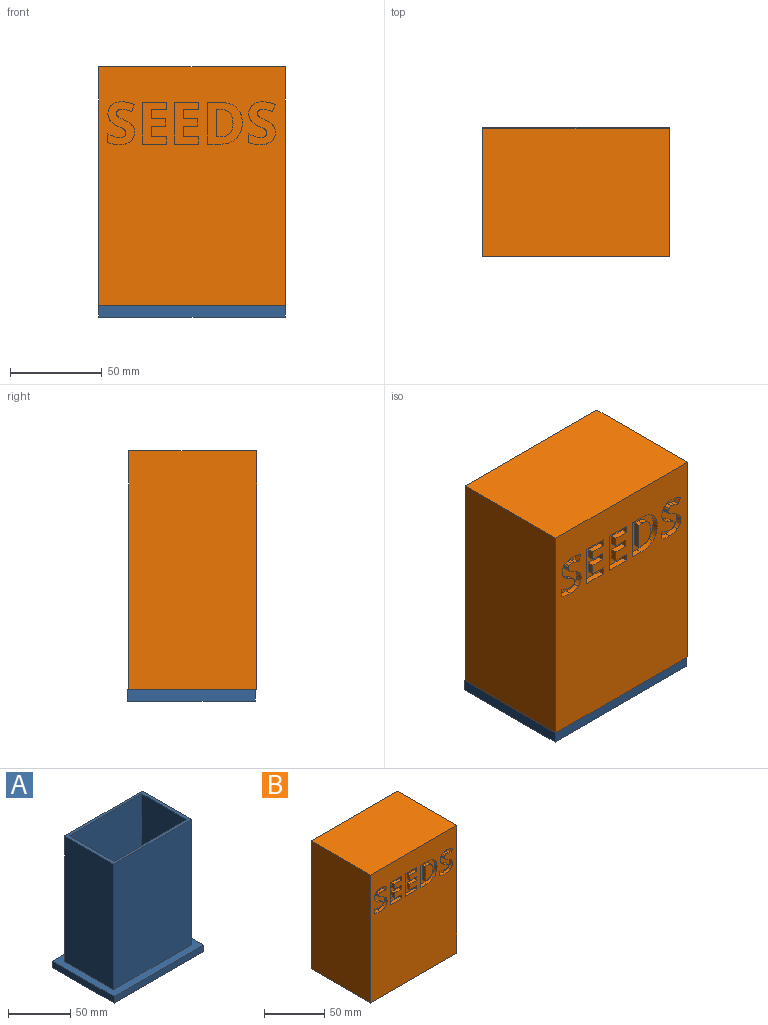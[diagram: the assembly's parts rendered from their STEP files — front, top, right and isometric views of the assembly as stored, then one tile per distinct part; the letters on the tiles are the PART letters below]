
ASSEMBLY  parts=2 mates=1
PART A: 16 faces, bbox 101.6x69.9x130.2 mm
  f0: plane 88.65x55.88mm, normal (0,0,1), area 760mm2, adj f1,f2,f3,f4,f11,f12,f14,f15
  f1: plane 123.83x55.88mm, normal (-1,0,0), area 6919.3mm2, adj f0,f3,f4,f5
  f2: plane 123.83x55.88mm, normal (1,0,0), area 6919.3mm2, adj f0,f3,f4,f5
  f3: plane 123.83x88.65mm, normal (0,-1,0), area 10976.6mm2, adj f0,f1,f2,f5
  f4: plane 123.83x88.65mm, normal (0,1,0), area 10976.6mm2, adj f0,f1,f2,f5
  f5: plane 101.6x69.85mm, normal (0,0,1), area 2143.2mm2, adj f1,f2,f3,f4,f6,f8,f9,f10
  f6: plane 69.85x6.35mm, normal (-1,0,0), area 443.5mm2, adj f5,f7,f9,f10
  f7: plane 101.6x69.85mm, normal (0,0,-1), area 7096.8mm2, adj f6,f8,f9,f10
  f8: plane 69.85x6.35mm, normal (1,0,0), area 443.5mm2, adj f5,f7,f9,f10
  f9: plane 101.6x6.35mm, normal (0,-1,0), area 645.2mm2, adj f5,f6,f7,f8
  f10: plane 101.6x6.35mm, normal (0,1,0), area 645.2mm2, adj f5,f6,f7,f8
  f11: plane 123.83x50.8mm, normal (-1,0,0), area 6290.3mm2, adj f0,f13,f14,f15
  f12: plane 123.83x50.8mm, normal (1,0,0), area 6290.3mm2, adj f0,f13,f14,f15
  f13: plane 82.55x50.8mm, normal (0,0,1), area 4193.5mm2, adj f11,f12,f14,f15
  f14: plane 123.83x82.55mm, normal (0,1,0), area 10221.8mm2, adj f0,f11,f12,f13
  f15: plane 123.83x82.55mm, normal (0,-1,0), area 10221.8mm2, adj f0,f11,f12,f13
PART B: 109 faces, bbox 101.6x69.9x130.2 mm
  f0: plane 130.18x101.6mm, normal (0,-1,0), area 12041.5mm2, adj f1,f2,f3,f4,f11,f12,f13,f14
  f1: plane 101.6x69.85mm, normal (0,0,-1), area 2016.1mm2, adj f0,f2,f4,f5,f6,f8,f9,f10
  f2: plane 130.18x69.85mm, normal (1,0,0), area 9092.7mm2, adj f0,f1,f3,f5
  f3: plane 101.6x69.85mm, normal (0,0,1), area 7096.8mm2, adj f0,f2,f4,f5
  f4: plane 130.18x69.85mm, normal (-1,0,0), area 9092.7mm2, adj f0,f1,f3,f5
  f5: plane 130.18x101.6mm, normal (0,1,0), area 13225.8mm2, adj f1,f2,f3,f4
  f6: plane 123.83x57.15mm, normal (-1,0,0), area 7076.6mm2, adj f1,f7,f9,f10
  f7: plane 88.9x57.15mm, normal (0,0,-1), area 5080.6mm2, adj f6,f8,f9,f10
  f8: plane 123.83x57.15mm, normal (1,0,0), area 7076.6mm2, adj f1,f7,f9,f10
  f9: plane 123.83x88.9mm, normal (0,-1,0), area 11008mm2, adj f1,f6,f7,f8
  f10: plane 123.83x88.9mm, normal (0,1,0), area 11008mm2, adj f1,f6,f7,f8
  f11: extruded ~4.86x3.18mm, area 17.6mm2, adj f0,f12,f38,f39
  f12: extruded ~3.76x3.18mm, area 12.7mm2, adj f0,f11,f13,f39
  f13: extruded ~4.38x3.18mm, area 17.1mm2, adj f0,f12,f14,f39
  f14: extruded ~3.18x3.06mm, area 11mm2, adj f0,f13,f15,f39
  f15: extruded ~3.18x0.94mm, area 4.2mm2, adj f0,f14,f16,f39
  f16: extruded ~3.18x1.11mm, area 3.7mm2, adj f0,f15,f17,f39
  f17: extruded ~3.18x1.66mm, area 6mm2, adj f0,f16,f18,f39
  f18: extruded ~3.18x2.1mm, area 7.1mm2, adj f0,f17,f19,f39
  f19: extruded ~3.18x2.34mm, area 7.5mm2, adj f0,f18,f20,f39
  f20: extruded ~3.18x3.01mm, area 10.1mm2, adj f0,f19,f21,f39
  f21: plane 3.76x3.18mm, normal (-0.92,0,0.38), area 12.9mm2, adj f0,f20,f22,f39
  f22: extruded ~3.37x3.18mm, area 11.4mm2, adj f0,f21,f23,f39
  f23: extruded ~3.39x3.18mm, area 10.9mm2, adj f0,f22,f24,f39
  f24: extruded ~5.66x3.18mm, area 19.2mm2, adj f0,f23,f25,f39
  f25: extruded ~4.75x3.18mm, area 17mm2, adj f0,f24,f26,f39
  f26: extruded ~3.18x2.8mm, area 9.2mm2, adj f0,f25,f27,f39
  f27: extruded ~3.18x2.1mm, area 8.6mm2, adj f0,f26,f28,f39
  f28: extruded ~3.18x3.13mm, area 11.6mm2, adj f0,f27,f29,f39
  f29: extruded ~3.18x2.95mm, area 10.6mm2, adj f0,f28,f30,f39
  f30: extruded ~3.18x1.1mm, area 4.8mm2, adj f0,f29,f31,f39
  f31: extruded ~3.18x1.19mm, area 4mm2, adj f0,f30,f32,f39
  f32: extruded ~3.18x1.81mm, area 6.6mm2, adj f0,f31,f33,f39
  f33: extruded ~3.18x2.43mm, area 8.1mm2, adj f0,f32,f34,f39
  f34: extruded ~3.18x2.92mm, area 9.4mm2, adj f0,f33,f35,f39
  f35: extruded ~3.9x3.18mm, area 13.2mm2, adj f0,f34,f36,f39
  f36: plane 4.48x3.18mm, normal (1,0,0), area 14.2mm2, adj f0,f35,f37,f39
  f37: extruded ~6.45x3.18mm, area 21.1mm2, adj f0,f36,f38,f39
  f38: extruded ~6.17x3.18mm, area 20.8mm2, adj f0,f11,f37,f39
  f39: plane 23.4x14.84mm, normal (0,-1,0), area 195.4mm2, adj f11,f12,f13,f14,f15,f16,f17,f18
  f40: extruded ~7.33x6.48mm, area 35.6mm2, adj f41,f51,f52,f108
  f41: extruded ~7.49x6.98mm, area 37.3mm2, adj f40,f42,f52,f108
  f42: plane 3.18x2.07mm, normal (0,0,-1), area 6.6mm2, adj f41,f43,f52,f108
  f43: plane 14.82x3.18mm, normal (-1,0,0), area 47.1mm2, adj f42,f51,f52,f108
  f44: extruded ~8.61x3.2mm, area 30mm2, adj f0,f45,f50,f52
  f45: extruded ~8.22x3.18mm, area 28.7mm2, adj f0,f44,f46,f52
  f46: extruded ~8.66x3.18mm, area 29.8mm2, adj f0,f45,f47,f52
  f47: plane 7.14x3.18mm, normal (0,0,-1), area 22.7mm2, adj f0,f46,f48,f52
  f48: plane 22.76x3.18mm, normal (1,0,0), area 72.3mm2, adj f0,f47,f49,f52
  f49: plane 6.45x3.18mm, normal (0,0,1), area 20.5mm2, adj f0,f48,f50,f52
  f50: extruded ~9.24x3.18mm, area 31.6mm2, adj f0,f44,f49,f52
  f51: plane 3.18x2.57mm, normal (0,0,1), area 8.1mm2, adj f40,f43,f52,f108
  f52: plane 22.76x18.89mm, normal (0,-1,0), area 263.8mm2, adj f40,f41,f42,f43,f44,f45,f46,f47
  f53: plane 13.11x3.18mm, normal (0,0,1), area 41.6mm2, adj f0,f54,f64,f65
  f54: plane 3.99x3.18mm, normal (-1,0,0), area 12.7mm2, adj f0,f53,f55,f65
  f55: plane 8.28x3.18mm, normal (0,0,-1), area 26.3mm2, adj f0,f54,f56,f65
  f56: plane 5.87x3.18mm, normal (-1,0,0), area 18.6mm2, adj f0,f55,f57,f65
  f57: plane 7.71x3.18mm, normal (0,0,1), area 24.5mm2, adj f0,f56,f58,f65
  f58: plane 3.96x3.18mm, normal (-1,0,0), area 12.6mm2, adj f0,f57,f59,f65
  f59: plane 7.71x3.18mm, normal (0,0,-1), area 24.5mm2, adj f0,f58,f60,f65
  f60: plane 5x3.18mm, normal (-1,0,0), area 15.9mm2, adj f0,f59,f61,f65
  f61: plane 8.28x3.18mm, normal (0,0,1), area 26.3mm2, adj f0,f60,f62,f65
  f62: plane 3.96x3.18mm, normal (-1,0,0), area 12.6mm2, adj f0,f61,f63,f65
  f63: plane 13.11x3.18mm, normal (0,0,-1), area 41.6mm2, adj f0,f62,f64,f65
  f64: plane 22.76x3.18mm, normal (1,0,0), area 72.3mm2, adj f0,f53,f63,f65
  f65: plane 22.76x13.11mm, normal (0,-1,0), area 206.1mm2, adj f53,f54,f55,f56,f57,f58,f59,f60
  f66: plane 13.11x3.18mm, normal (0,0,1), area 41.6mm2, adj f0,f67,f77,f78
  f67: plane 3.99x3.18mm, normal (-1,0,0), area 12.7mm2, adj f0,f66,f68,f78
  f68: plane 8.28x3.18mm, normal (0,0,-1), area 26.3mm2, adj f0,f67,f69,f78
  f69: plane 5.87x3.18mm, normal (-1,0,0), area 18.6mm2, adj f0,f68,f70,f78
  f70: plane 7.71x3.18mm, normal (0,0,1), area 24.5mm2, adj f0,f69,f71,f78
  f71: plane 3.96x3.18mm, normal (-1,0,0), area 12.6mm2, adj f0,f70,f72,f78
  f72: plane 7.71x3.18mm, normal (0,0,-1), area 24.5mm2, adj f0,f71,f73,f78
  f73: plane 5x3.18mm, normal (-1,0,0), area 15.9mm2, adj f0,f72,f74,f78
  f74: plane 8.28x3.18mm, normal (0,0,1), area 26.3mm2, adj f0,f73,f75,f78
  f75: plane 3.96x3.18mm, normal (-1,0,0), area 12.6mm2, adj f0,f74,f76,f78
  f76: plane 13.11x3.18mm, normal (0,0,-1), area 41.6mm2, adj f0,f75,f77,f78
  f77: plane 22.76x3.18mm, normal (1,0,0), area 72.3mm2, adj f0,f66,f76,f78
  f78: plane 22.76x13.11mm, normal (0,-1,0), area 206.1mm2, adj f66,f67,f68,f69,f70,f71,f72,f73
  f79: extruded ~4.86x3.18mm, area 17.6mm2, adj f0,f80,f106,f107
  f80: extruded ~3.76x3.18mm, area 12.7mm2, adj f0,f79,f81,f107
  f81: extruded ~4.38x3.18mm, area 17.1mm2, adj f0,f80,f82,f107
  f82: extruded ~3.18x3.06mm, area 11mm2, adj f0,f81,f83,f107
  f83: extruded ~3.18x0.94mm, area 4.2mm2, adj f0,f82,f84,f107
  f84: extruded ~3.18x1.11mm, area 3.7mm2, adj f0,f83,f85,f107
  f85: extruded ~3.18x1.66mm, area 6mm2, adj f0,f84,f86,f107
  f86: extruded ~3.18x2.1mm, area 7.1mm2, adj f0,f85,f87,f107
  f87: extruded ~3.18x2.34mm, area 7.5mm2, adj f0,f86,f88,f107
  f88: extruded ~3.18x3.01mm, area 10.1mm2, adj f0,f87,f89,f107
  f89: plane 3.76x3.18mm, normal (-0.92,0,0.38), area 12.9mm2, adj f0,f88,f90,f107
  f90: extruded ~3.37x3.18mm, area 11.4mm2, adj f0,f89,f91,f107
  f91: extruded ~3.39x3.18mm, area 10.9mm2, adj f0,f90,f92,f107
  f92: extruded ~5.66x3.18mm, area 19.2mm2, adj f0,f91,f93,f107
  f93: extruded ~4.75x3.18mm, area 17mm2, adj f0,f92,f94,f107
  f94: extruded ~3.18x2.8mm, area 9.2mm2, adj f0,f93,f95,f107
  f95: extruded ~3.18x2.1mm, area 8.6mm2, adj f0,f94,f96,f107
  f96: extruded ~3.18x3.13mm, area 11.6mm2, adj f0,f95,f97,f107
  f97: extruded ~3.18x2.95mm, area 10.6mm2, adj f0,f96,f98,f107
  f98: extruded ~3.18x1.1mm, area 4.8mm2, adj f0,f97,f99,f107
  f99: extruded ~3.18x1.19mm, area 4mm2, adj f0,f98,f100,f107
  f100: extruded ~3.18x1.81mm, area 6.6mm2, adj f0,f99,f101,f107
  f101: extruded ~3.18x2.43mm, area 8.1mm2, adj f0,f100,f102,f107
  f102: extruded ~3.18x2.92mm, area 9.4mm2, adj f0,f101,f103,f107
  f103: extruded ~3.9x3.18mm, area 13.2mm2, adj f0,f102,f104,f107
  f104: plane 4.48x3.18mm, normal (1,0,0), area 14.2mm2, adj f0,f103,f105,f107
  f105: extruded ~6.45x3.18mm, area 21.1mm2, adj f0,f104,f106,f107
  f106: extruded ~6.17x3.18mm, area 20.8mm2, adj f0,f79,f105,f107
  f107: plane 23.4x14.84mm, normal (0,-1,0), area 195.4mm2, adj f79,f80,f81,f82,f83,f84,f85,f86
  f108: plane 14.82x9.04mm, normal (0,-1,0), area 117.4mm2, adj f40,f41,f42,f43,f51
PLACE A t=(-16.23,386.23,105.87)mm
PLACE B t=(-16.23,385.59,109.04)mm
MATE fastened B.f9 <-> A.f4  axis (0,-1,0) through (-16.23,414.17,105.87)mm
